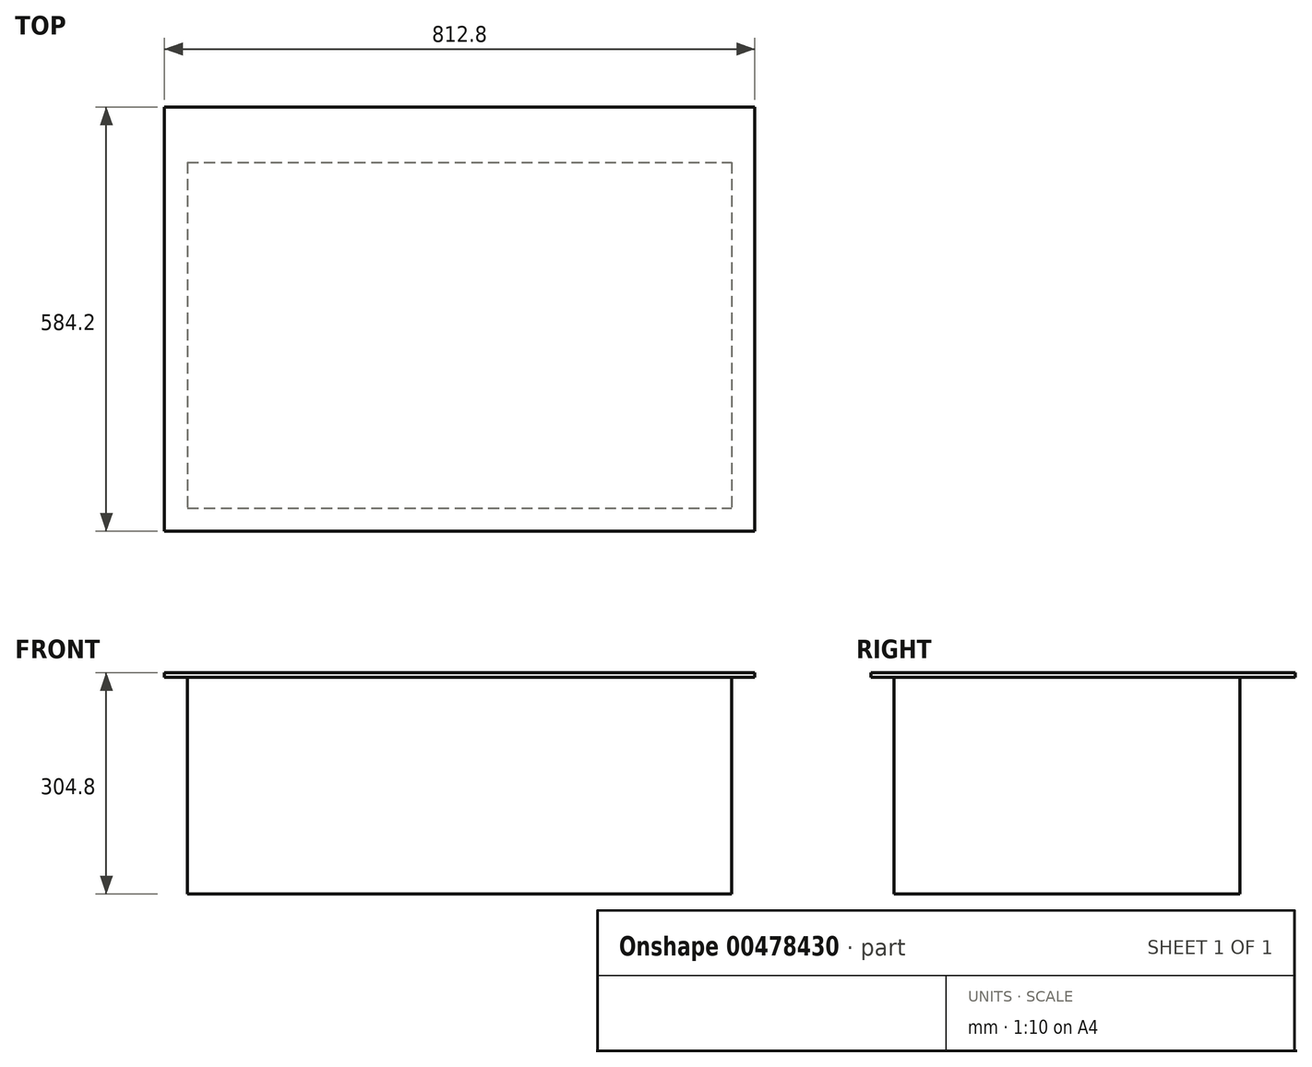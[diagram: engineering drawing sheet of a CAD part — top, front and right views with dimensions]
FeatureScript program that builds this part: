
annotation { "Feature Type Name" : "Feature", "Feature Type Description" : "" }
export const myFeature = defineFeature(function(context is Context, id is Id, definition is map)
    precondition{}
    {
        {
            var Q0;
            Q0=qCreatedBy(makeId("Top.planeOp"),FACE);
            var sketch = newSketch(context, id + "F0", { "sketchPlane" : qUnion([Q0])});
            skLineSegment(sketch, "E0.bottom", {"start": v(-406.4, 292.1) * mm, "end": v(406.4, 292.1) * mm});
            skLineSegment(sketch, "E0.top", {"start": v(-406.4, -292.1) * mm, "end": v(406.4, -292.1) * mm});
            skLineSegment(sketch, "E0.left", {"start": v(-406.4, 292.1) * mm, "end": v(-406.4, -292.1) * mm});
            skLineSegment(sketch, "E0.right", {"start": v(406.4, 292.1) * mm, "end": v(406.4, -292.1) * mm});
            skPoint(sketch, "E0.middle", {"position": v(0, 0) * mm});
            skSolve(sketch);
        }
        {
            var Q0;
            Q0=makeQuery(id+"F0.imprint","IMPRINT",FACE,{"disambiguationData":[TD([[makeQuery(id+"F0.imprint","IMPRINT",EDGE,{"derivedFrom":sQuery(id+"F0.wireOp",EDGE,"E0.bottom")}),-1.0]])]});
            extrude(context, id + "F1", {"entities" : qUnion([Q0]), "depth" : 304.8 * mm, "offsetDistance" : 25.4 * mm});
        }
        {
            var Q0;
            Q0=makeQuery(id+"F1.opExtrude","SWEPT_FACE",FACE,{"disambiguationData":[OSD([sQuery(id+"F0.wireOp",EDGE,"E0.top")])]});
            var sketch = newSketch(context, id + "F2", { "sketchPlane" : qUnion([Q0])});
            skLineSegment(sketch, "E1.bottom", {"start": v(-406.4, 298.45) * mm, "end": v(406.4, 298.45) * mm});
            skLineSegment(sketch, "E1.top", {"start": v(-406.4, 0) * mm, "end": v(406.4, 0) * mm});
            skLineSegment(sketch, "E1.left", {"start": v(-406.4, 298.45) * mm, "end": v(-406.4, 0) * mm});
            skLineSegment(sketch, "E1.right", {"start": v(406.4, 298.45) * mm, "end": v(406.4, 0) * mm});
            skSolve(sketch);
        }
        {
            var Q0;
            Q0 = qSketchRegion(id + "F2", true);
            extrude(context, id + "F3", {"entities" : qUnion([Q0]), "operationType" : NewBodyOperationType.REMOVE, "oppositeDirection" : true, "depth" : 31.75 * mm, "offsetDistance" : 25.4 * mm});
        }
        {
            var Q0;
            Q0=makeQuery(id+"F1.opExtrude","SWEPT_FACE",FACE,{"disambiguationData":[OSD([sQuery(id+"F0.wireOp",EDGE,"E0.bottom")])]});
            var sketch = newSketch(context, id + "F4", { "sketchPlane" : qUnion([Q0])});
            skLineSegment(sketch, "E2.bottom", {"start": v(-406.4, 298.45) * mm, "end": v(406.4, 298.45) * mm});
            skLineSegment(sketch, "E2.top", {"start": v(-406.4, 0) * mm, "end": v(406.4, 0) * mm});
            skLineSegment(sketch, "E2.left", {"start": v(-406.4, 298.45) * mm, "end": v(-406.4, 0) * mm});
            skLineSegment(sketch, "E2.right", {"start": v(406.4, 298.45) * mm, "end": v(406.4, 0) * mm});
            skSolve(sketch);
        }
        {
            var Q0;
            Q0 = qSketchRegion(id + "F4", true);
            extrude(context, id + "F5", {"entities" : qUnion([Q0]), "operationType" : NewBodyOperationType.REMOVE, "oppositeDirection" : true, "depth" : 76.2 * mm, "offsetDistance" : 25.4 * mm});
        }
        {
            var Q0;
            Q0=makeQuery(id+"F1.opExtrude","SWEPT_FACE",FACE,{"disambiguationData":[OSD([sQuery(id+"F0.wireOp",EDGE,"E0.right")])]});
            var sketch = newSketch(context, id + "F6", { "sketchPlane" : qUnion([Q0])});
            skLineSegment(sketch, "E3.bottom", {"start": v(-260.35, 298.45) * mm, "end": v(215.9, 298.45) * mm});
            skLineSegment(sketch, "E3.top", {"start": v(-260.35, 0) * mm, "end": v(215.9, 0) * mm});
            skLineSegment(sketch, "E3.left", {"start": v(-260.35, 298.45) * mm, "end": v(-260.35, 0) * mm});
            skLineSegment(sketch, "E3.right", {"start": v(215.9, 298.45) * mm, "end": v(215.9, 0) * mm});
            skSolve(sketch);
        }
        {
            var Q0;
            Q0 = qSketchRegion(id + "F6", true);
            extrude(context, id + "F7", {"entities" : qUnion([Q0]), "operationType" : NewBodyOperationType.REMOVE, "oppositeDirection" : true, "depth" : 31.75 * mm, "offsetDistance" : 25.4 * mm});
        }
        {
            var Q0;
            Q0=makeQuery(id+"F1.opExtrude","SWEPT_FACE",FACE,{"disambiguationData":[OSD([sQuery(id+"F0.wireOp",EDGE,"E0.left")])]});
            var sketch = newSketch(context, id + "F8", { "sketchPlane" : qUnion([Q0])});
            skLineSegment(sketch, "E4.bottom", {"start": v(-215.9, 0) * mm, "end": v(260.35, 0) * mm});
            skLineSegment(sketch, "E4.top", {"start": v(-215.9, 298.45) * mm, "end": v(260.35, 298.45) * mm});
            skLineSegment(sketch, "E4.left", {"start": v(-215.9, 0) * mm, "end": v(-215.9, 298.45) * mm});
            skLineSegment(sketch, "E4.right", {"start": v(260.35, 0) * mm, "end": v(260.35, 298.45) * mm});
            skSolve(sketch);
        }
        {
            var Q0;
            Q0 = qSketchRegion(id + "F8", true);
            extrude(context, id + "F9", {"entities" : qUnion([Q0]), "operationType" : NewBodyOperationType.REMOVE, "oppositeDirection" : true, "depth" : 31.75 * mm, "offsetDistance" : 25.4 * mm});
        }
    });
